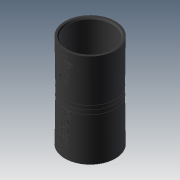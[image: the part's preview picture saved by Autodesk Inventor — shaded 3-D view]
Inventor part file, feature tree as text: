
AUTODESK INVENTOR PART (.ipt)
format: ipt  version: 2020 (Build 240168000, 168)  size: 400,384 bytes
history: native  units: mm
features: sketch x3, revolve x2, chamfer x2, plane x1, extrude x1
ambient origin geometry x8: Origin, YZ Plane, XZ Plane, XY Plane, X Axis, Y Axis, Z Axis, Center Point
bodies: Solid1 (feature_tree)
feature tree (9):
  revolve  "Revolution1"  Angle=90.0deg
  plane  "Work Plane1"
  extrude  "Extrusion1"  Depth=10.0mm TaperAngle=0.0deg
  revolve  "Revolution2"  [1 undecoded]
  chamfer  "Chamfer2"  Distance=31.340941mm
  chamfer  "Chamfer3"  Distance=0.15mm
  sketch  "Sketch2"  dims[d0=11.25mm d1=25.0mm d2=10.5mm d3=3.5mm d4=2.0mm d5=15.80796mm d6=1.35mm d7=2.0mm d8=1.35mm d9=0.0mm d10=90.0deg]
  sketch  "Sketch3"  dims[d11=12.75mm d12=10.0mm d13=0.0mm]
  sketch  "Sketch4"  dims[d14=31.340941mm d15=31.340941mm d16=31.340941mm d17=0.15mm d18=90.0deg d22=0.6mm d23=2.0mm d24=45.0deg d25=0.15mm d26=2.0mm d27=45.0deg]
note: 1 required parameter value undecoded (feature->parameter linkage not recoverable at this tier; creation-order binding heuristic only, values carry confidence <= 0.55)
